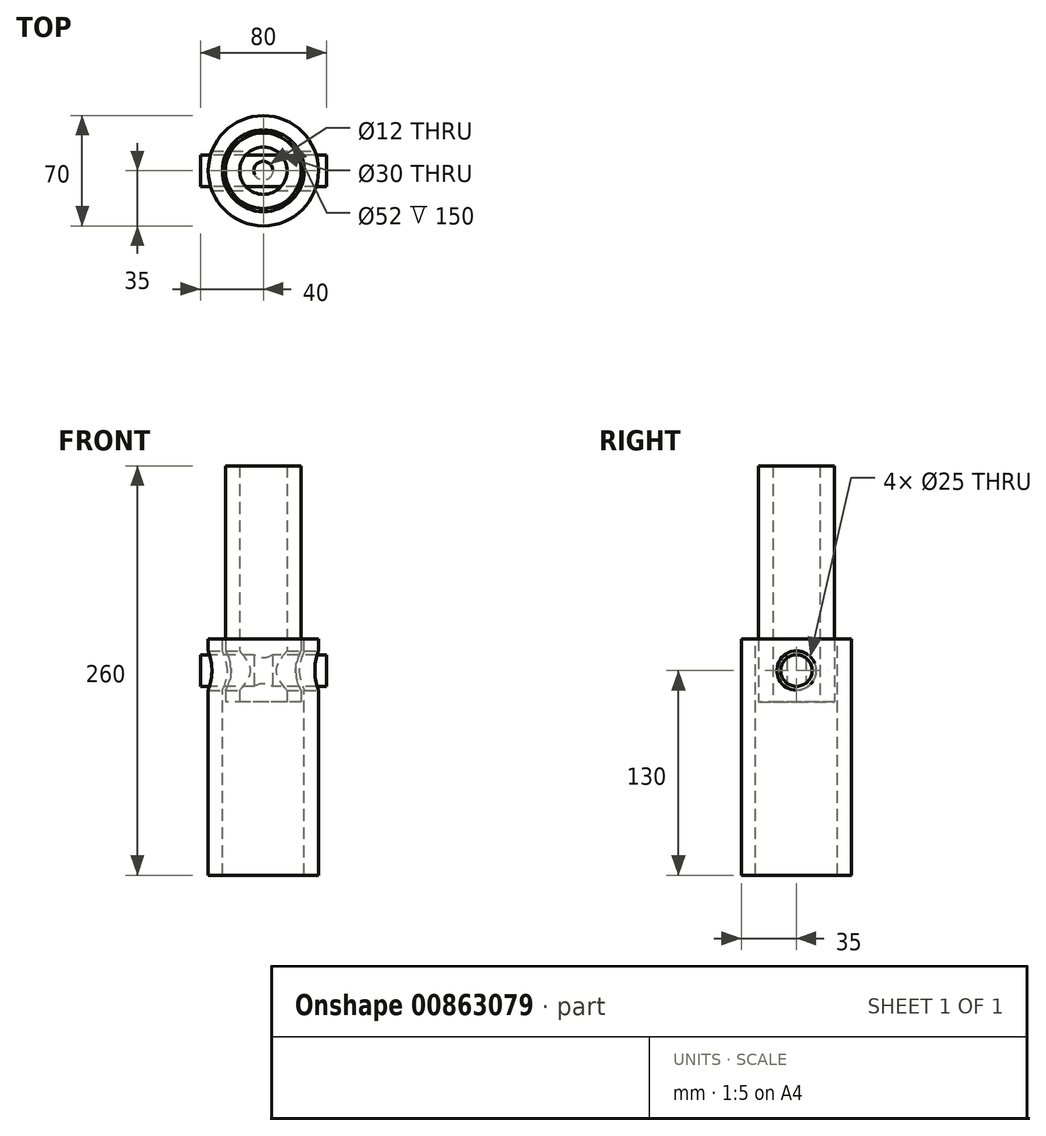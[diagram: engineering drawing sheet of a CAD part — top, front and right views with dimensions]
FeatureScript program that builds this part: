
annotation { "Feature Type Name" : "Feature", "Feature Type Description" : "" }
export const myFeature = defineFeature(function(context is Context, id is Id, definition is map)
    precondition{}
    {
        {
            var Q0;
            Q0=qCreatedBy(makeId("Top.planeOp"),FACE);
            var sketch = newSketch(context, id + "F0", { "sketchPlane" : qUnion([Q0])});
            skCircle(sketch, "E0", {"center": v(0, 0) * mm, "radius": 26 * mm});
            skCircle(sketch, "E1", {"center": v(0, 0) * mm, "radius": 35 * mm});
            skSolve(sketch);
        }
        {
            var Q0;
            Q0 = qSketchRegion(id + "F0", true);
            extrude(context, id + "F1", {"entities" : qUnion([Q0]), "oppositeDirection" : true, "depth" : 150 * mm, "offsetDistance" : 25 * mm});
        }
        {
            var Q0;
            Q0=qCreatedBy(makeId("Top.planeOp"),FACE);
            cPlane(context, id + "F2", {"entities" : qUnion([Q0]), "cplaneType" : CPlaneType.OFFSET, "offset" : 40 * mm, "oppositeDirection" : true, "width" : 150 * mm, "height" : 150 * mm});
        }
        {
            var Q0;
            Q0=qCreatedBy(id+"F2.planeOp",FACE);
            var sketch = newSketch(context, id + "F3", { "sketchPlane" : qUnion([Q0])});
            skCircle(sketch, "E2", {"center": v(0, 0) * mm, "radius": 24 * mm});
            skCircle(sketch, "E3", {"center": v(0, 0) * mm, "radius": 15 * mm});
            skSolve(sketch);
        }
        {
            var Q0;
            Q0 = qSketchRegion(id + "F3", true);
            extrude(context, id + "F4", {"entities" : qUnion([Q0]), "depth" : 150 * mm, "offsetDistance" : 25 * mm});
        }
        {
            var Q0;
            Q0=qCreatedBy(makeId("Right.planeOp"),FACE);
            var sketch = newSketch(context, id + "F5", { "sketchPlane" : qUnion([Q0])});
            skCircle(sketch, "E4", {"center": v(0, -20) * mm, "radius": 12.5 * mm});
            skSolve(sketch);
        }
        {
            var Q0;
            Q0 = qSketchRegion(id + "F5", true);
            extrude(context, id + "F6", {"entities" : qUnion([Q0]), "operationType" : NewBodyOperationType.REMOVE, "endBound" : BoundingType.THROUGH_ALL, "oppositeDirection" : true, "depth" : 25 * mm, "offsetDistance" : 25 * mm, "hasSecondDirection" : true, "secondDirectionBound" : SecondDirectionBoundingType.THROUGH_ALL, "secondDirectionOppositeDirection" : false, "secondDirectionDepth" : 25 * mm});
        }
        {
            var Q0;
            Q0=qCreatedBy(makeId("Right.planeOp"),FACE);
            var sketch = newSketch(context, id + "F7", { "sketchPlane" : qUnion([Q0])});
            skCircle(sketch, "E5.0", {"center": v(0, -20) * mm, "radius": 12.5 * mm, "construction": true});
            skCircle(sketch, "E6", {"center": v(0, -20) * mm, "radius": 10 * mm});
            skSolve(sketch);
        }
        {
            var Q0;
            Q0 = qSketchRegion(id + "F7", true);
            extrude(context, id + "F8", {"entities" : qUnion([Q0]), "depth" : 40 * mm, "offsetDistance" : 25 * mm, "hasSecondDirection" : true, "secondDirectionOppositeDirection" : true, "secondDirectionDepth" : 40 * mm});
        }
        {
            var Q0;
            Q0=qCreatedBy(makeId("Top.planeOp"),FACE);
            var sketch = newSketch(context, id + "F9", { "sketchPlane" : qUnion([Q0])});
            skCircle(sketch, "E7", {"center": v(0, 0) * mm, "radius": 6 * mm});
            skSolve(sketch);
        }
        {
            var Q0;
            Q0 = qSketchRegion(id + "F9", true);
            extrude(context, id + "F10", {"entities" : qUnion([Q0]), "operationType" : NewBodyOperationType.REMOVE, "endBound" : BoundingType.THROUGH_ALL, "depth" : 25 * mm, "offsetDistance" : 25 * mm, "hasSecondDirection" : true, "secondDirectionBound" : SecondDirectionBoundingType.THROUGH_ALL, "secondDirectionOppositeDirection" : true, "secondDirectionDepth" : 25 * mm});
        }
    });
